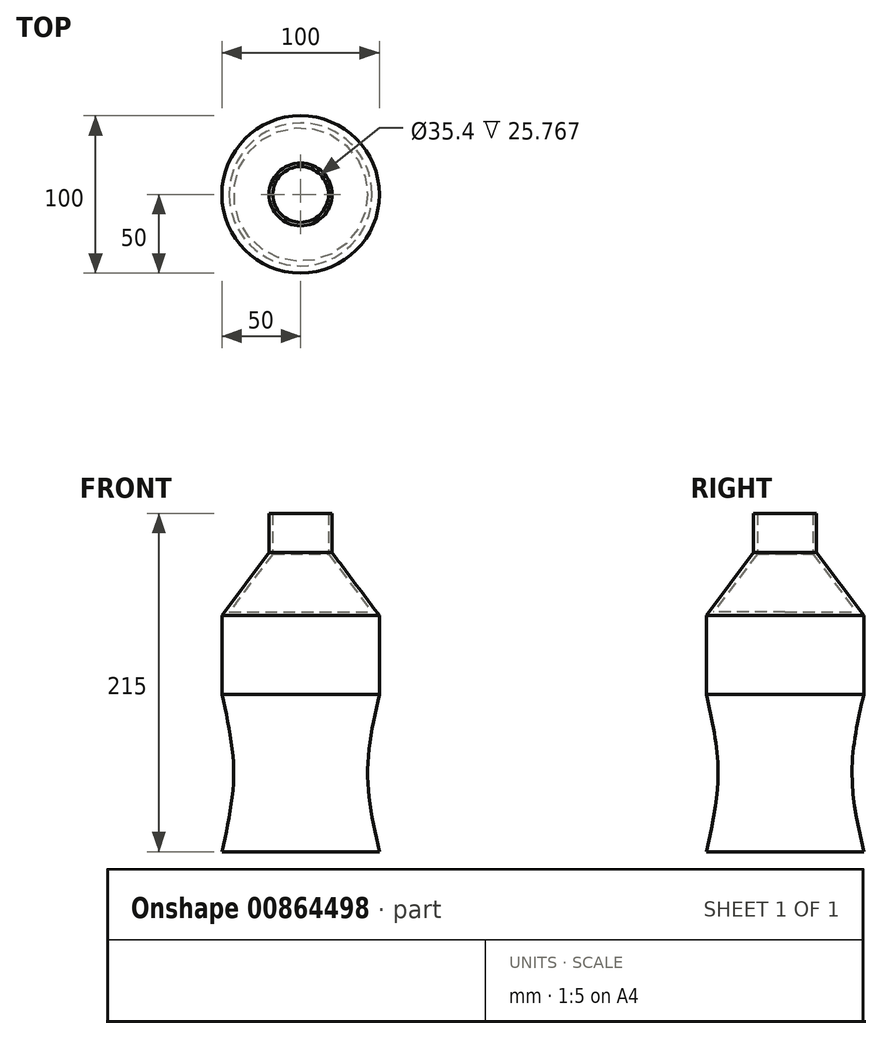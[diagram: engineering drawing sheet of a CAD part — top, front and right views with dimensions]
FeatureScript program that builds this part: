
annotation { "Feature Type Name" : "Feature", "Feature Type Description" : "" }
export const myFeature = defineFeature(function(context is Context, id is Id, definition is map)
    precondition{}
    {
        {
            var Q0;
            Q0=qCreatedBy(makeId("Top.planeOp"),FACE);
            var sketch = newSketch(context, id + "F0", { "sketchPlane" : qUnion([Q0])});
            skCircle(sketch, "E0", {"center": v(0, 0) * mm, "radius": 50 * mm});
            skSolve(sketch);
        }
        {
            var Q0;
            Q0=qCreatedBy(makeId("Top.planeOp"),FACE);
            cPlane(context, id + "F1", {"entities" : qUnion([Q0]), "cplaneType" : CPlaneType.OFFSET, "offset" : 50 * mm, "width" : 150 * mm, "height" : 150 * mm});
        }
        {
            var Q0;
            Q0=qCreatedBy(id+"F1.planeOp",FACE);
            var sketch = newSketch(context, id + "F2", { "sketchPlane" : qUnion([Q0])});
            skCircle(sketch, "E1", {"center": v(0, 0) * mm, "radius": 42.5 * mm});
            skSolve(sketch);
        }
        {
            var Q0;
            Q0=qCreatedBy(id+"F1.planeOp",FACE);
            cPlane(context, id + "F3", {"entities" : qUnion([Q0]), "cplaneType" : CPlaneType.OFFSET, "offset" : 50 * mm, "width" : 150 * mm, "height" : 150 * mm});
        }
        {
            var Q0;
            Q0=qCreatedBy(id+"F3.planeOp",FACE);
            cPlane(context, id + "F4", {"entities" : qUnion([Q0]), "cplaneType" : CPlaneType.OFFSET, "offset" : 50 * mm, "width" : 150 * mm, "height" : 150 * mm});
        }
        {
            var Q0;
            Q0=qCreatedBy(id+"F3.planeOp",FACE);
            var sketch = newSketch(context, id + "F5", { "sketchPlane" : qUnion([Q0])});
            skCircle(sketch, "E2", {"center": v(0, 0) * mm, "radius": 50 * mm});
            skSolve(sketch);
        }
        {
            var Q0;
            Q0=qCreatedBy(id+"F4.planeOp",FACE);
            var sketch = newSketch(context, id + "F6", { "sketchPlane" : qUnion([Q0])});
            skCircle(sketch, "E3", {"center": v(0, 0) * mm, "radius": 50 * mm});
            skSolve(sketch);
        }
        {
            var Q0;
            Q0=qCreatedBy(id+"F4.planeOp",FACE);
            cPlane(context, id + "F7", {"entities" : qUnion([Q0]), "cplaneType" : CPlaneType.OFFSET, "offset" : 40 * mm, "width" : 150 * mm, "height" : 150 * mm});
        }
        {
            var Q0;
            Q0=qCreatedBy(id+"F7.planeOp",FACE);
            var sketch = newSketch(context, id + "F8", { "sketchPlane" : qUnion([Q0])});
            skCircle(sketch, "E4", {"center": v(0, 0) * mm, "radius": 20 * mm});
            skSolve(sketch);
        }
        {
            var Q0;
            Q0=makeQuery(id+"F0.imprint","IMPRINT",FACE,{"disambiguationData":[TD([[makeQuery(id+"F0.imprint","IMPRINT",EDGE,{"derivedFrom":sQuery(id+"F0.wireOp",EDGE,"E0")}),1.0]])]});
            var Q1;
            Q1=makeQuery(id+"F2.imprint","IMPRINT",FACE,{"disambiguationData":[TD([[makeQuery(id+"F2.imprint","IMPRINT",EDGE,{"derivedFrom":sQuery(id+"F2.wireOp",EDGE,"E1")}),1.0]])]});
            var Q2;
            Q2=makeQuery(id+"F5.imprint","IMPRINT",FACE,{"disambiguationData":[TD([[makeQuery(id+"F5.imprint","IMPRINT",EDGE,{"derivedFrom":sQuery(id+"F5.wireOp",EDGE,"E2")}),1.0]])]});
            loft(context, id + "F9", {"sheetProfilesArray" : [{ "sheetProfileEntities" : qUnion([Q0]) }, { "sheetProfileEntities" : qUnion([Q1]) }, { "sheetProfileEntities" : qUnion([Q2]) }]});
        }
        {
            var Q0;
            Q0=makeQuery(id+"F9.opLoft","CAP_FACE",FACE,{"disambiguationData":[OSD([makeQuery(id+"F5.imprint","IMPRINT",FACE,{"disambiguationData":[TD([[makeQuery(id+"F5.imprint","IMPRINT",EDGE,{"derivedFrom":sQuery(id+"F5.wireOp",EDGE,"E2")}),1.0]])]})])],"isStart":true});
            extrude(context, id + "F10", {"entities" : qUnion([Q0]), "operationType" : NewBodyOperationType.ADD, "depth" : 50 * mm, "offsetDistance" : 25 * mm});
        }
        {
            var Q0;
            Q0=makeQuery(id+"F6.imprint","IMPRINT",FACE,{"disambiguationData":[TD([[makeQuery(id+"F6.imprint","IMPRINT",EDGE,{"derivedFrom":sQuery(id+"F6.wireOp",EDGE,"E3")}),1.0]])]});
            var Q1;
            Q1=makeQuery(id+"F8.imprint","IMPRINT",FACE,{"disambiguationData":[TD([[makeQuery(id+"F8.imprint","IMPRINT",EDGE,{"derivedFrom":sQuery(id+"F8.wireOp",EDGE,"E4")}),1.0]])]});
            loft(context, id + "F11", {"sheetProfilesArray" : [{ "sheetProfileEntities" : qUnion([Q0]) }, { "sheetProfileEntities" : qUnion([Q1]) }]});
        }
        {
            var Q0;
            Q0=makeQuery(id+"F8.imprint","IMPRINT",FACE,{"disambiguationData":[TD([[makeQuery(id+"F8.imprint","IMPRINT",EDGE,{"derivedFrom":sQuery(id+"F8.wireOp",EDGE,"E4")}),1.0]])]});
            extrude(context, id + "F12", {"entities" : qUnion([Q0]), "operationType" : NewBodyOperationType.ADD, "depth" : 25 * mm, "offsetDistance" : 25 * mm});
        }
        {
            var Q0;
            Q0=makeQuery(id+"F12.opExtrude","CAP_FACE",FACE,{"disambiguationData":[OSD([sQuery(id+"F8.wireOp",EDGE,"E4")])],"isStart":false});
            shell(context, id + "F13", {"entities" : qUnion([Q0]), "thickness" : 2.3 * mm});
        }
    });
